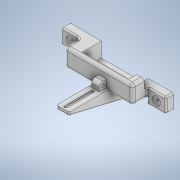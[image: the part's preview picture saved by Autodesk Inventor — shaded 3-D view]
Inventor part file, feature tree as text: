
AUTODESK INVENTOR PART (.ipt)
format: ipt  version: 2020 (Build 240168000, 168)  size: 524,800 bytes
history: native  units: mm
features: extrude x19, sketch x17, projected_geometry x16, fillet x7, mirror x2, plane x1, split x1
ambient origin geometry x8: Origin, YZ Plane, XZ Plane, XY Plane, X Axis, Y Axis, Z Axis, Center Point
bodies: Solid1 (feature_tree)
feature tree (63):
  extrude  "Extrusion1"  Depth=50.0mm
  sketch  "Sketch2"  dims[d2=31.0mm d3=15.5mm]
  extrude  "Extrusion2"  Depth=15.5mm
  extrude  "Extrusion3"  Depth=63.0mm
  mirror  "Mirror1"
  extrude  "Extrusion5"  Depth=11.0mm
  extrude  "Extrusion6"  Depth=20.0mm TaperAngle=0.0deg
  extrude  "Extrusion8"  Depth=11.5mm
  mirror  "Mirror2"
  extrude  "Extrusion9"  Depth=2.0mm TaperAngle=0.0deg
  extrude  "Extrusion13"  Depth=85.0mm
  sketch  "Sketch17"  dims[d22=100.0mm d23=85.0mm]
  extrude  "Extrusion15"  Depth=28.0mm
  extrude  "Extrusion16"  Depth=10.0mm TaperAngle=0.0deg
  extrude  "Extrusion17"  Depth=7.0mm
  extrude  "Extrusion18"  Depth=10.0mm TaperAngle=0.0deg
  extrude  "Extrusion21"  Depth=5.0mm
  extrude  "Extrusion22"  Depth=10.0mm
  fillet  "Fillet5"  Radius=20.0mm
  fillet  "Fillet6"  Radius=85.0mm
  fillet  "Fillet7"  Radius=12.0mm
  fillet  "Fillet9"  Radius=10.0mm
  plane  "Work Plane1"
  split  "Split1"
  extrude  "Extrusion23"  Depth=0.5641mm TaperAngle=0.0deg
  extrude  "Extrusion24"  Depth=4.0mm
  sketch  "Sketch30"  dims[d75=3.564mm d76=0.0mm d77=4.0mm]
  extrude  "Extrusion25"  Depth=4.0mm
  extrude  "Extrusion26"  Depth=10.0mm
  fillet  "Fillet10"  Radius=2.0mm
  fillet  "Fillet11"  Radius=4.0mm
  fillet  "Fillet12"  Radius=2.0mm
  extrude  "Extrusion27"  Depth=10.0mm
  sketch  "Sketch1"  dims[d0=100.0mm d1=50.0mm]
  projected_geometry  "Projected Loop1"
  sketch  "Sketch4"  dims[d4=26.0mm d5=63.0mm]
  projected_geometry  "Projected Loop3"
  sketch  "Sketch5"  dims[d6=31.5mm d7=11.0mm]
  sketch  "Sketch7"  dims[d8=25.0mm d9=20.0mm d10=0.0mm]
  projected_geometry  "Projected Loop5"
  sketch  "Sketch11"  dims[d11=3.5mm d12=11.5mm]
  projected_geometry  "Projected Loop11"
  sketch  "Sketch16"  dims[d13=0.0mm d14=0.0mm d15=2.0mm d16=0.0mm]
  projected_geometry  "Projected Loop19"
  projected_geometry  "Projected Loop20"
  projected_geometry  "Projected Loop21"
  sketch  "Sketch18"  dims[d24=5.0mm d25=0.0mm d26=28.0mm]
  projected_geometry  "Projected Loop22"
  sketch  "Sketch21"  dims[d27=10.0mm d28=57.0mm d29=0.0mm]
  projected_geometry  "Projected Loop23"
  sketch  "Sketch22"  dims[d33=24.25mm d34=0.0mm d39=7.0mm]
  projected_geometry  "Projected Loop24"
  sketch  "Sketch25"  dims[d40=5.0mm d41=10.0mm d42=0.0mm]
  projected_geometry  "Projected Loop27"
  sketch  "Sketch26"  dims[d51=5.0mm d52=0.0mm d53=5.0mm]
  projected_geometry  "Projected Loop28"
  sketch  "Sketch27"  dims[d54=4.2mm d55=5.0mm d59=20.0mm d60=85.0mm d61=12.0mm d62=0.0mm d63=10.0mm d64=0.0mm]
  projected_geometry  "Projected Loop29"
  projected_geometry  "Projected Loop30"
  sketch  "Sketch29"  dims[d65=268.25mm d66=0.0mm d68=0.5641mm d69=0.0mm]
  projected_geometry  "Projected Loop31"
  sketch  "Sketch31"  dims[d78=14.0mm d79=4.0mm d80=8.564053mm d81=2.0mm d82=0.0mm d83=4.0mm d84=2.0mm d85=5.0mm d87=2.0mm d88=-8.75mm d92=15.0mm d93=24.0mm d94=0.0mm d95=8.0mm d96=20.0mm d97=0.0mm d98=11.0mm d99=20.0mm d100=25.0mm d101=0.0mm d102=12.5mm d103=10.0mm d104=3.5mm d105=11.5mm d106=211.75mm d107=0.0mm d108=2.0mm d109=0.0mm d110=2.0mm d111=4.0mm d112=2.0mm d113=10.0mm d114=0.0mm d36=0.5mm d37=0.872665mm d38=0.5mm]
  projected_geometry  "Projected Loop32"
